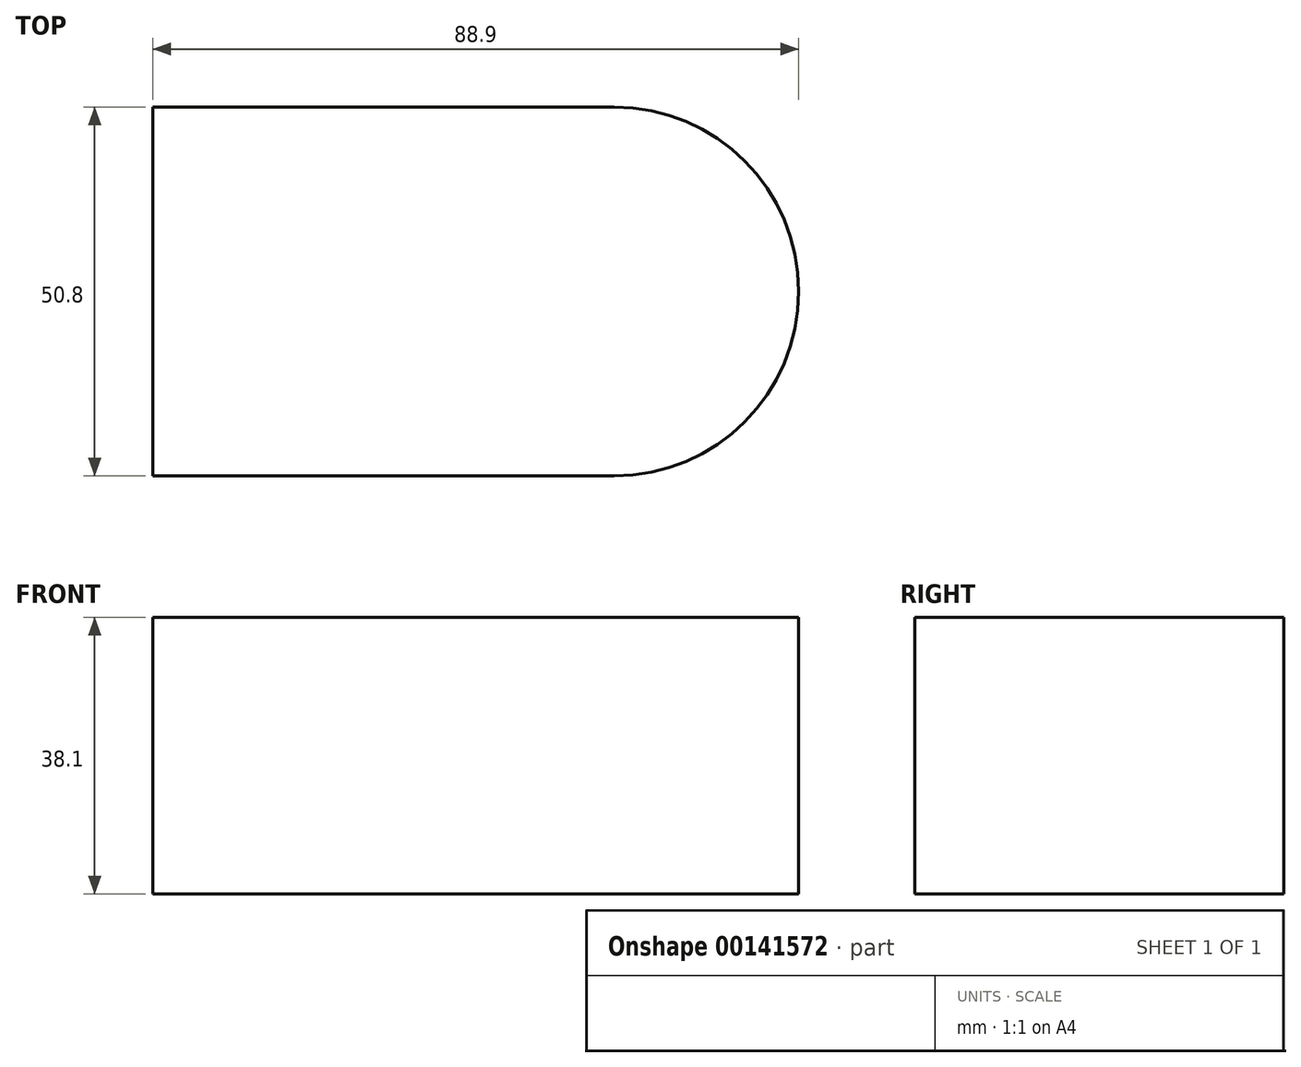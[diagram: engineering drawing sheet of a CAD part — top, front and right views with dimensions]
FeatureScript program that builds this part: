
annotation { "Feature Type Name" : "Feature", "Feature Type Description" : "" }
export const myFeature = defineFeature(function(context is Context, id is Id, definition is map)
    precondition{}
    {
        {
            var Q0;
            Q0=qCreatedBy(makeId("Top.planeOp"),FACE);
            var sketch = newSketch(context, id + "F0", { "sketchPlane" : qUnion([Q0])});
            skLineSegment(sketch, "E0.bottom", {"start": v(-37.84, 41.48) * mm, "end": v(25.66, 41.48) * mm});
            skLineSegment(sketch, "E0.top", {"start": v(-37.84, -9.32) * mm, "end": v(25.66, -9.32) * mm});
            skLineSegment(sketch, "E0.left", {"start": v(-37.84, 41.48) * mm, "end": v(-37.84, -9.32) * mm});
            skLineSegment(sketch, "E0.right", {"start": v(25.66, 41.48) * mm, "end": v(25.66, -9.32) * mm});
            skArc(sketch, "E1", {"start": v(25.66, -9.32) * mm, "mid": v(51.06, 16.08) * mm, "end": v(25.66, 41.48) * mm});
            skSolve(sketch);
        }
        {
            var Q0;
            Q0=makeQuery(id+"F0.imprint","IMPRINT",FACE,{"disambiguationData":[TD([[makeQuery(id+"F0.imprint","IMPRINT",EDGE,{"derivedFrom":sQuery(id+"F0.wireOp",EDGE,"E0.bottom")}),-1.0]])]});
            extrude(context, id + "F1", {"entities" : qUnion([Q0]), "depth" : 38.1 * mm});
        }
        {
            var Q0;
            Q0 = qSketchRegion(id + "F0", true);
            extrude(context, id + "F2", {"entities" : qUnion([Q0]), "operationType" : NewBodyOperationType.ADD, "depth" : 38.1 * mm});
        }
    });
